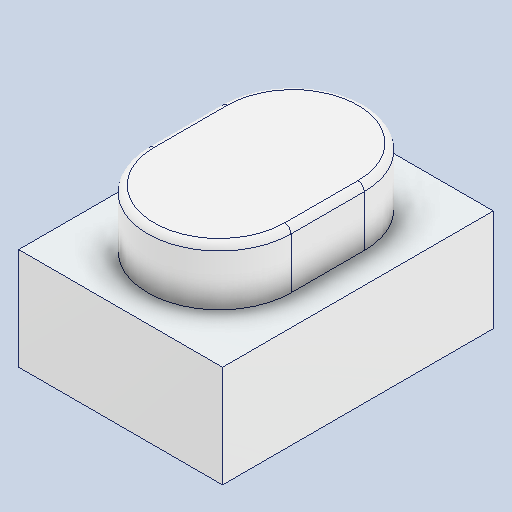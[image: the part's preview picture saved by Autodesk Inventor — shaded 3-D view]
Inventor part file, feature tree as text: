
AUTODESK INVENTOR PART (.ipt)
format: ipt  version: 2022 (Build 260153000, 153)  size: 124,416 bytes
history: imported  units: in
note: dims shown in document units (in); Inventor stores cm internally (conversion verified against a paired STEP export)
features: imported_body x1
ambient origin geometry x8: Origin, YZ Plane, XZ Plane, XY Plane, X Axis, Y Axis, Z Axis, Center Point
bodies: Solid1 (imported_parasolid)
feature tree (1):
  imported_body  NMx_Import_Brep_tag  [imported B-rep: ~15 faces, bbox_mm=[3.2, 2.5, 4.25]]
